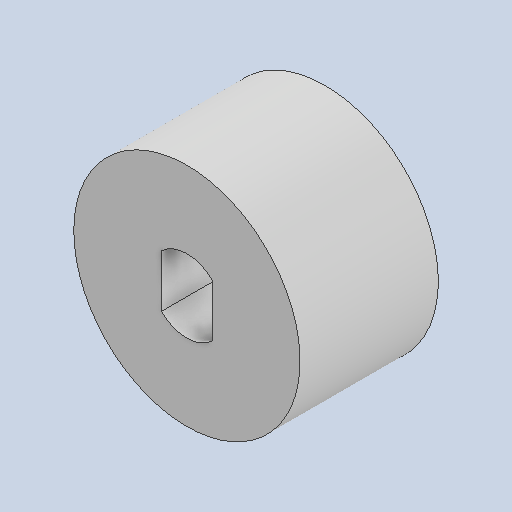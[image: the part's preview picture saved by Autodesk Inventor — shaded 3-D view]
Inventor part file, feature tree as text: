
AUTODESK INVENTOR PART (.ipt)
format: ipt  version: 2022.3 (Build 263350000, 350)  size: 151,040 bytes
history: native  units: mm
features: reference x3, other x3, extrude x2, sketch x2, projected_geometry x1
ambient origin geometry x8: Origin, YZ Plane, XZ Plane, XY Plane, X Axis, Y Axis, Z Axis, Center Point
bodies: Solid1 (feature_tree)
feature tree (11):
  extrude  "Extrusion1"  Depth=10.0mm TaperAngle=0.0deg
  extrude  "Extrusion2"  TaperAngle=0.0deg  [1 undecoded]
  sketch  "Sketch1"  dims[d0=1.0mm d1=10.0mm d2=0.0mm]
  reference  "Reference1"
  reference  "Reference2"
  reference  "Reference3"
  sketch  "Sketch2"  dims[d3=0.5mm d4=0.0mm d5=0.0mm]
  projected_geometry  "Projected Loop1"
  other  "<userpath>\Documents\Inventor\NanoSumo\Przekładnia.iam"
  other  "Przekładnia.iam"
  other  "Moteur - Engrenage 1:1"
note: 1 required parameter value undecoded (feature->parameter linkage not recoverable at this tier; creation-order binding heuristic only, values carry confidence <= 0.55)
